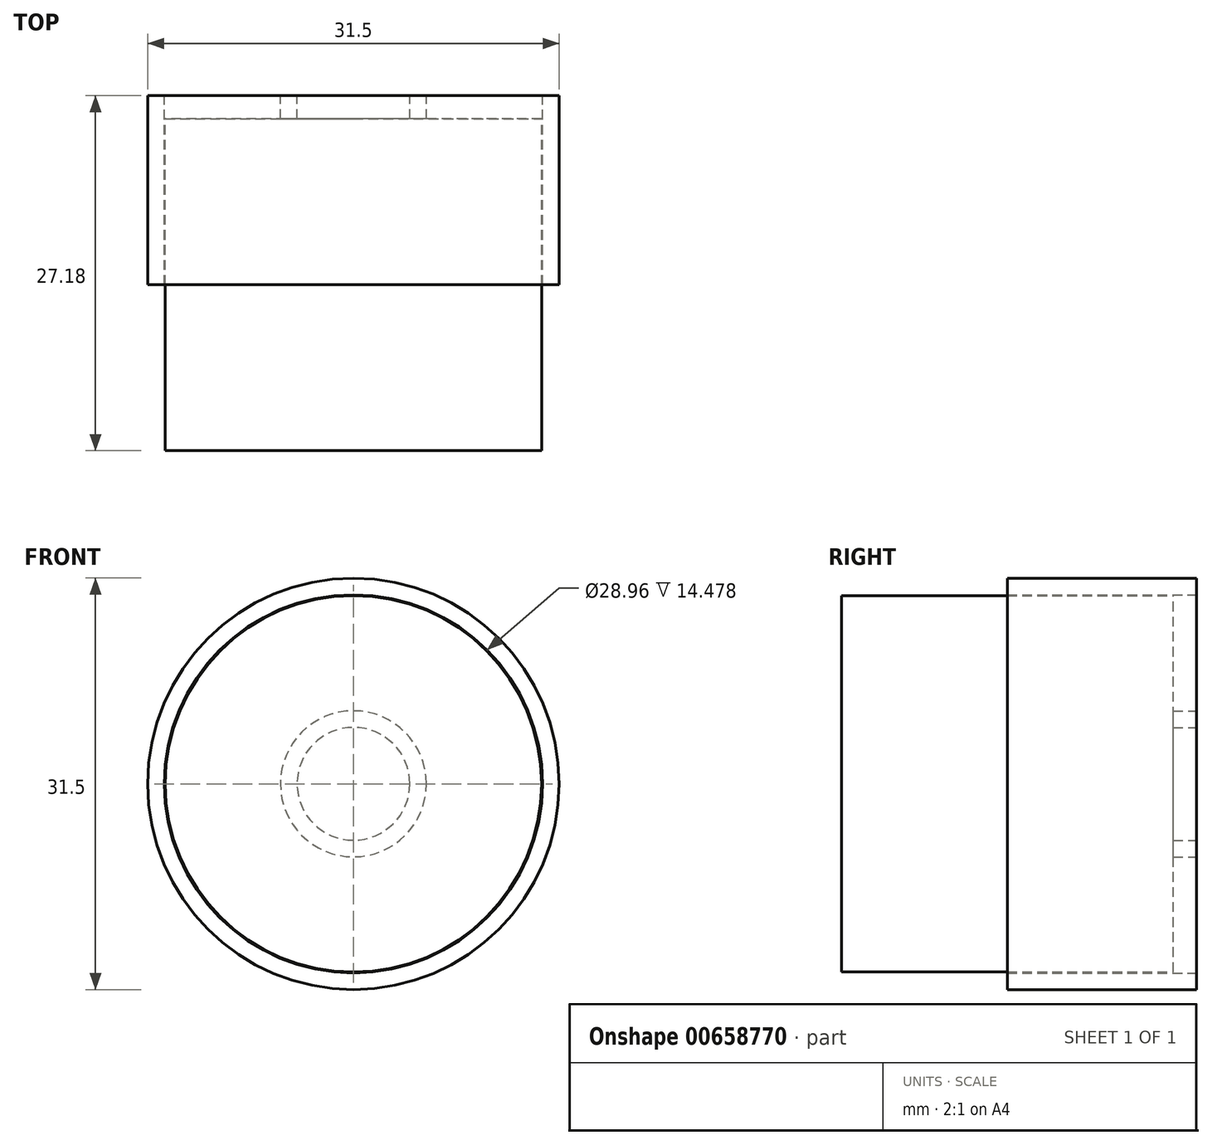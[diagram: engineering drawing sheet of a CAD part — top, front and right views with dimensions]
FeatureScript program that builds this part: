
annotation { "Feature Type Name" : "Feature", "Feature Type Description" : "" }
export const myFeature = defineFeature(function(context is Context, id is Id, definition is map)
    precondition{}
    {
        {
            var Q0;
            Q0=qCreatedBy(makeId("Front.planeOp"),FACE);
            var sketch = newSketch(context, id + "F0", { "sketchPlane" : qUnion([Q0])});
            skCircle(sketch, "E0", {"center": v(0, 0) * mm, "radius": 5.59 * mm});
            skCircle(sketch, "E1.0", {"center": v(0, 0) * mm, "radius": 4.32 * mm});
            skCircle(sketch, "E2", {"center": v(0, 0) * mm, "radius": 14.48 * mm});
            skCircle(sketch, "E3.0", {"center": v(0, 0) * mm, "radius": 15.75 * mm});
            skSolve(sketch);
        }
        {
            var Q0;
            Q0=makeQuery(id+"F0.imprint","IMPRINT",FACE,{"disambiguationData":[TD([[makeQuery(id+"F0.imprint","IMPRINT",EDGE,{"derivedFrom":sQuery(id+"F0.wireOp",EDGE,"E0")}),1.0]])]});
            var Q1;
            Q1=makeQuery(id+"F0.imprint","IMPRINT",FACE,{"disambiguationData":[TD([[makeQuery(id+"F0.imprint","IMPRINT",EDGE,{"derivedFrom":sQuery(id+"F0.wireOp",EDGE,"E2")}),-1.0]])]});
            extrude(context, id + "F1", {"entities" : qUnion([Q0, Q1]), "endBound" : BoundingType.SYMMETRIC, "depth" : 14.48 * mm, "offsetDistance" : 25.4 * mm});
        }
        {
            var Q0;
            Q0=makeQuery(id+"F1.opExtrude","CAP_FACE",FACE,{"disambiguationData":[OSD([sQuery(id+"F0.wireOp",EDGE,"E2"),sQuery(id+"F0.wireOp",EDGE,"E3.0")])],"isStart":false});
            var sketch = newSketch(context, id + "F2", { "sketchPlane" : qUnion([Q0])});
            skCircle(sketch, "E4", {"center": v(0, 0) * mm, "radius": 14.4 * mm});
            skSolve(sketch);
        }
        {
            var Q0;
            Q0=makeQuery(id+"F2.imprint","IMPRINT",FACE,{"disambiguationData":[TD([[makeQuery(id+"F2.imprint","IMPRINT",EDGE,{"derivedFrom":sQuery(id+"F2.wireOp",EDGE,"E4")}),1.0]])]});
            extrude(context, id + "F3", {"entities" : qUnion([Q0]), "operationType" : NewBodyOperationType.ADD, "endBound" : BoundingType.SYMMETRIC, "depth" : 25.4 * mm, "offsetDistance" : 25.4 * mm});
        }
    });
